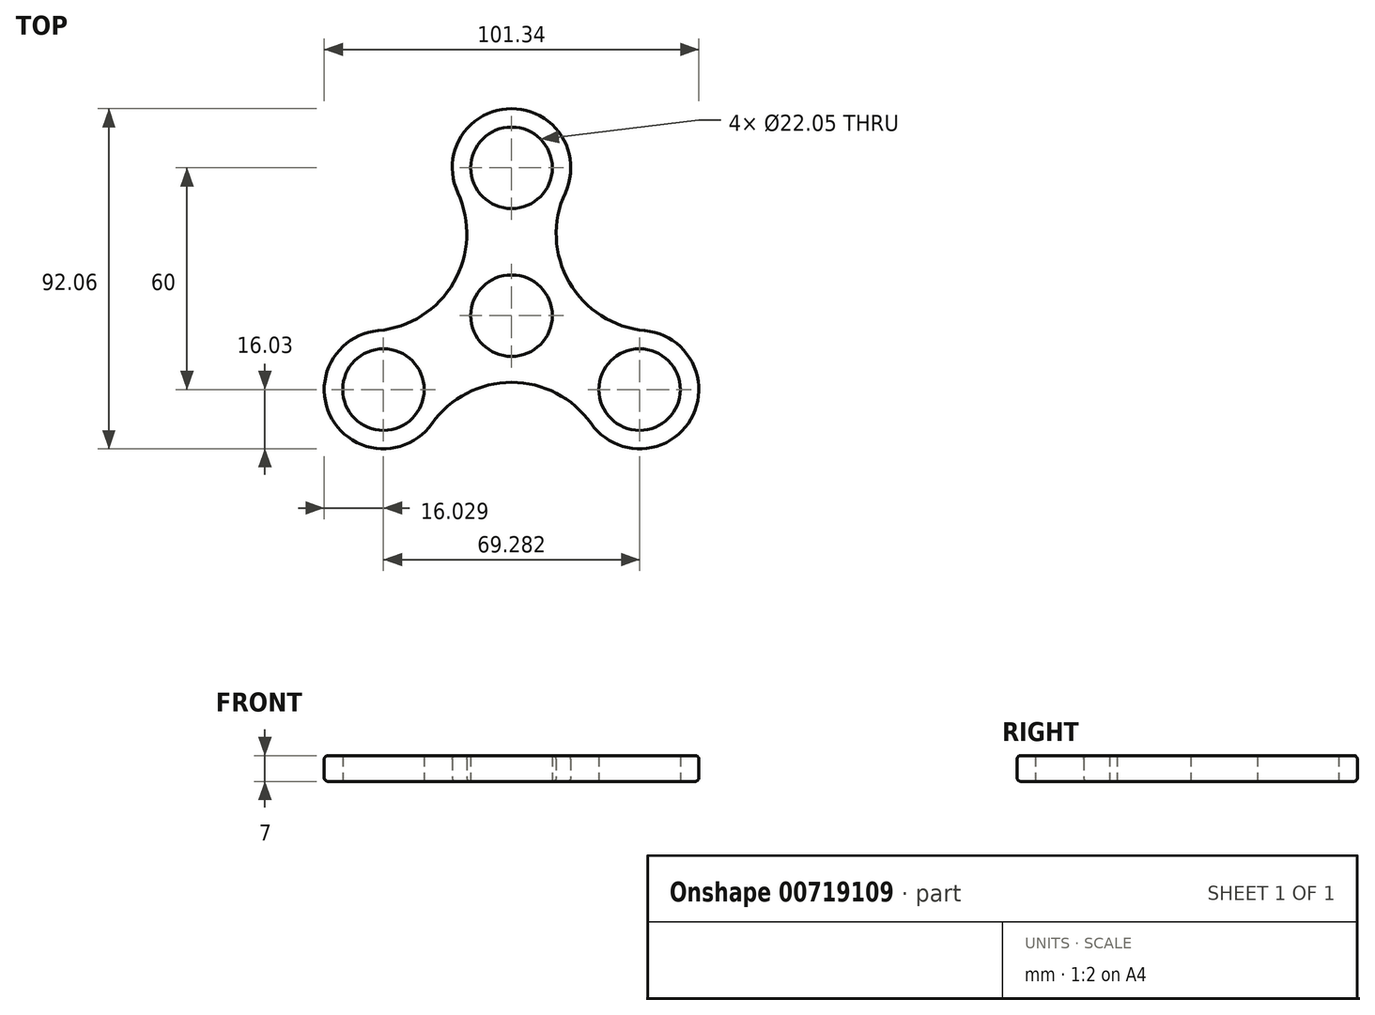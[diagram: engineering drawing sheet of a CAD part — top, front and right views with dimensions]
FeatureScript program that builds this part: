
annotation { "Feature Type Name" : "Feature", "Feature Type Description" : "" }
export const myFeature = defineFeature(function(context is Context, id is Id, definition is map)
    precondition{}
    {
        {
            var Q0;
            Q0=qCreatedBy(makeId("Top.planeOp"),FACE);
            var sketch = newSketch(context, id + "F0", { "sketchPlane" : qUnion([Q0])});
            skCircle(sketch, "E0", {"center": v(0, 0) * mm, "radius": 11.03 * mm});
            skCircle(sketch, "E1", {"center": v(0, 40) * mm, "radius": 11.03 * mm});
            skCircle(sketch, "E2.0", {"center": v(0, 40) * mm, "radius": 16.02 * mm});
            skCircle(sketch, "E3.0", {"center": v(0, 0) * mm, "radius": 18.02 * mm});
            skArc(sketch, "E4", {"start": v(-15.6, 9.01) * mm, "mid": v(-12.11, 21) * mm, "end": v(-14.53, 33.25) * mm});
            skLineSegment(sketch, "E5", {"start": v(0, -22.67) * mm, "end": v(0, 73.3) * mm, "construction": true});
            skArc(sketch, "E6.MirrorCS", {"start": v(15.6, 9.01) * mm, "mid": v(12.11, 21) * mm, "end": v(14.53, 33.25) * mm});
            skArc(sketch, "E7.1.0", {"start": v(0, -18.02) * mm, "mid": v(-12.13, -20.99) * mm, "end": v(-21.53, -29.21) * mm});
            skArc(sketch, "E7.1.1", {"start": v(-15.61, 9.01) * mm, "mid": v(-24.24, -0.01) * mm, "end": v(-36.06, -4.04) * mm});
            skCircle(sketch, "E7.1.2", {"center": v(-34.64, -20) * mm, "radius": 16.02 * mm});
            skCircle(sketch, "E7.1.3", {"center": v(-34.64, -20) * mm, "radius": 11.03 * mm});
            skArc(sketch, "E7.2.0", {"start": v(15.61, 9.01) * mm, "mid": v(24.24, -0.01) * mm, "end": v(36.06, -4.04) * mm});
            skArc(sketch, "E7.2.1", {"start": v(0, -18.02) * mm, "mid": v(12.13, -20.99) * mm, "end": v(21.53, -29.21) * mm});
            skCircle(sketch, "E7.2.2", {"center": v(34.64, -20) * mm, "radius": 16.02 * mm});
            skCircle(sketch, "E7.2.3", {"center": v(34.64, -20) * mm, "radius": 11.03 * mm});
            skSolve(sketch);
        }
        {
            var Q0;
            Q0 = qSketchRegion(id + "F0", true);
            var Q1;
            Q1=makeQuery(id+"F0.imprint","IMPRINT",FACE,{"disambiguationData":[TD([[makeQuery(id+"F0.imprint","IMPRINT",EDGE,{"derivedFrom":sQuery(id+"F0.wireOp",EDGE,"E0")}),-1.0]])]});
            extrude(context, id + "F1", {"entities" : qUnion([Q0, Q1]), "depth" : 7 * mm, "offsetDistance" : 25 * mm});
        }
        {
            var Q0;
            Q0=makeQuery(id+"F1.opExtrude","SWEPT_FACE",FACE,{"disambiguationData":[OSD([sQuery(id+"F0.wireOp",EDGE,"E2.0")])]});
            var Q1;
            Q1=makeQuery(id+"F1.opExtrude","SWEPT_FACE",FACE,{"disambiguationData":[OSD([sQuery(id+"F0.wireOp",EDGE,"E4")])]});
            var Q2;
            Q2=makeQuery(id+"F1.opExtrude","SWEPT_FACE",FACE,{"disambiguationData":[OSD([sQuery(id+"F0.wireOp",EDGE,"E7.1.1")])]});
            var Q3;
            Q3=makeQuery(id+"F1.opExtrude","SWEPT_FACE",FACE,{"disambiguationData":[OSD([sQuery(id+"F0.wireOp",EDGE,"E7.1.2")])]});
            var Q4;
            Q4=makeQuery(id+"F1.opExtrude","SWEPT_FACE",FACE,{"disambiguationData":[OSD([sQuery(id+"F0.wireOp",EDGE,"E7.2.1")])]});
            fillet(context, id + "F2", {"entities" : qUnion([Q0, Q1, Q2, Q3, Q4]), "radius" : 1 * mm, "tangentPropagation" : true, "allowEdgeOverflow" : false});
        }
    });
